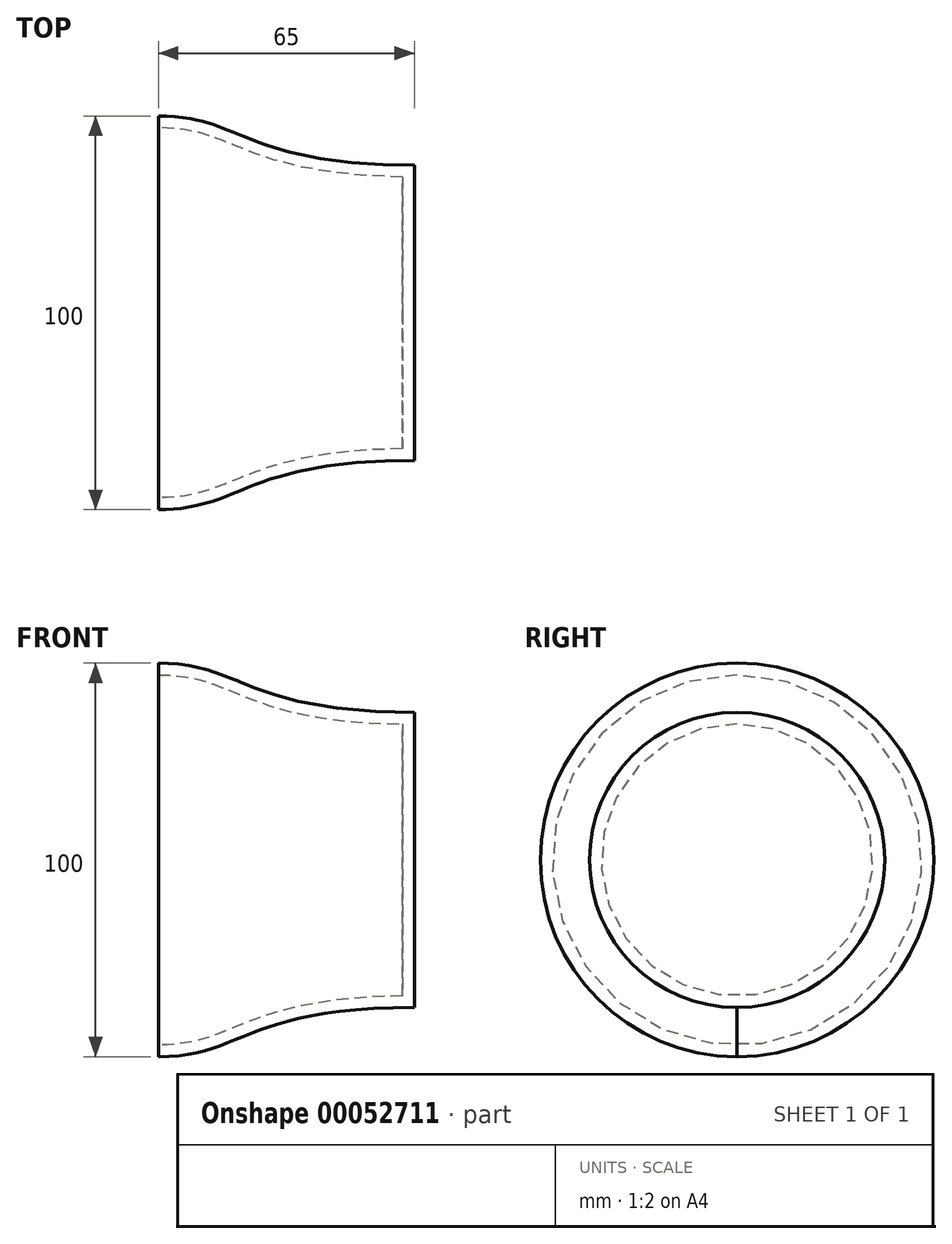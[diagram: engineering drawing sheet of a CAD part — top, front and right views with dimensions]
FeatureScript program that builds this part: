
annotation { "Feature Type Name" : "Feature", "Feature Type Description" : "" }
export const myFeature = defineFeature(function(context is Context, id is Id, definition is map)
    precondition{}
    {
        {
            var Q0;
            Q0=qCreatedBy(makeId("Right.planeOp"),FACE);
            cPlane(context, id + "F0", {"entities" : qUnion([Q0]), "cplaneType" : CPlaneType.OFFSET, "offset" : 65 * mm, "width" : 150 * mm, "height" : 150 * mm});
        }
        {
            var Q0;
            Q0=qCreatedBy(makeId("Right.planeOp"),FACE);
            var sketch = newSketch(context, id + "F1", { "sketchPlane" : qUnion([Q0])});
            skCircle(sketch, "E0", {"center": v(0, 0) * mm, "radius": 50 * mm});
            skSolve(sketch);
        }
        {
            var Q0;
            Q0=qCreatedBy(id+"F0.planeOp",FACE);
            var sketch = newSketch(context, id + "F2", { "sketchPlane" : qUnion([Q0])});
            skCircle(sketch, "E1", {"center": v(0, 0) * mm, "radius": 37.5 * mm});
            skSolve(sketch);
        }
        {
            var Q0;
            Q0=makeQuery(id+"F1.imprint","IMPRINT",FACE,{"disambiguationData":[TD([[makeQuery(id+"F1.imprint","IMPRINT",EDGE,{"derivedFrom":sQuery(id+"F1.wireOp",EDGE,"E0")}),1.0]])]});
            var Q1;
            Q1=makeQuery(id+"F2.imprint","IMPRINT",FACE,{"disambiguationData":[TD([[makeQuery(id+"F2.imprint","IMPRINT",EDGE,{"derivedFrom":sQuery(id+"F2.wireOp",EDGE,"E1")}),1.0]])]});
            loft(context, id + "F3", {"startCondition" : LoftEndDerivativeType.NORMAL_TO_PROFILE, "startMagnitude" : 1, "endCondition" : LoftEndDerivativeType.NORMAL_TO_PROFILE, "endMagnitude" : 2, "sheetProfilesArray" : [{ "sheetProfileEntities" : qUnion([Q0]) }, { "sheetProfileEntities" : qUnion([Q1]) }]});
        }
        {
            var Q0;
            Q0=makeQuery(id+"F3.opLoft","CAP_FACE",FACE,{"disambiguationData":[OSD([makeQuery(id+"F2.imprint","IMPRINT",FACE,{"disambiguationData":[TD([[makeQuery(id+"F2.imprint","IMPRINT",EDGE,{"derivedFrom":sQuery(id+"F2.wireOp",EDGE,"E1")}),1.0]])]})])],"isStart":true});
            var Q1;
            Q1=makeQuery(id+"F3.opLoft","CAP_FACE",FACE,{"disambiguationData":[OSD([makeQuery(id+"F1.imprint","IMPRINT",FACE,{"disambiguationData":[TD([[makeQuery(id+"F1.imprint","IMPRINT",EDGE,{"derivedFrom":sQuery(id+"F1.wireOp",EDGE,"E0")}),1.0]])]})])],"isStart":true});
            shell(context, id + "F4", {"entities" : qUnion([Q0, Q1]), "thickness" : 3 * mm});
        }
        {
            var Q0;
            Q0=qCreatedBy(makeId("Top.planeOp"),FACE);
            var sketch = newSketch(context, id + "F5", { "sketchPlane" : qUnion([Q0])});
            skLineSegment(sketch, "E2", {"start": v(-46.23, 0) * mm, "end": v(103.56, 0) * mm, "construction": true});
            skSolve(sketch);
        }
    });
